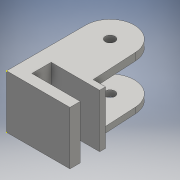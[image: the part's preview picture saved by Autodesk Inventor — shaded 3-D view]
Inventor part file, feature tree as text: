
AUTODESK INVENTOR PART (.ipt)
format: ipt  version: 2016 (Build 200138000, 138)  size: 136,192 bytes
history: native  units: mm
features: sketch x9, extrude x4
ambient origin geometry x8: Origin, YZ Plane, XZ Plane, XY Plane, X Axis, Y Axis, Z Axis, Center Point
bodies: Solid1 (feature_tree)
feature tree (13):
  extrude  "Extrusion1"  Depth=8.0mm
  extrude  "Extrusion2"  Depth=10.0mm
  extrude  "Extrusion3"  Depth=19.989431mm
  sketch  "Sketch4"  dims[d8=22.0mm d9=0.0mm d10=22.0mm d11=0.0mm]
  sketch  "Sketch5"  dims[d12=22.0mm d13=0.0mm]
  sketch  "Sketch6"  dims[d14=28.0mm]
  sketch  "Sketch7"  dims[d15=22.0mm d16=0.0mm]
  sketch  "Sketch8"
  extrude  "Extrusion4"  Depth=22.0mm TaperAngle=0.0deg
  sketch  "Sketch1"  dims[d0=20.0mm d1=8.0mm]
  sketch  "Sketch2"  dims[d3=4.0mm d4=10.0mm]
  sketch  "Sketch3"  dims[d5=18.0mm d7=19.989431mm]
  sketch  "Sketch9"
